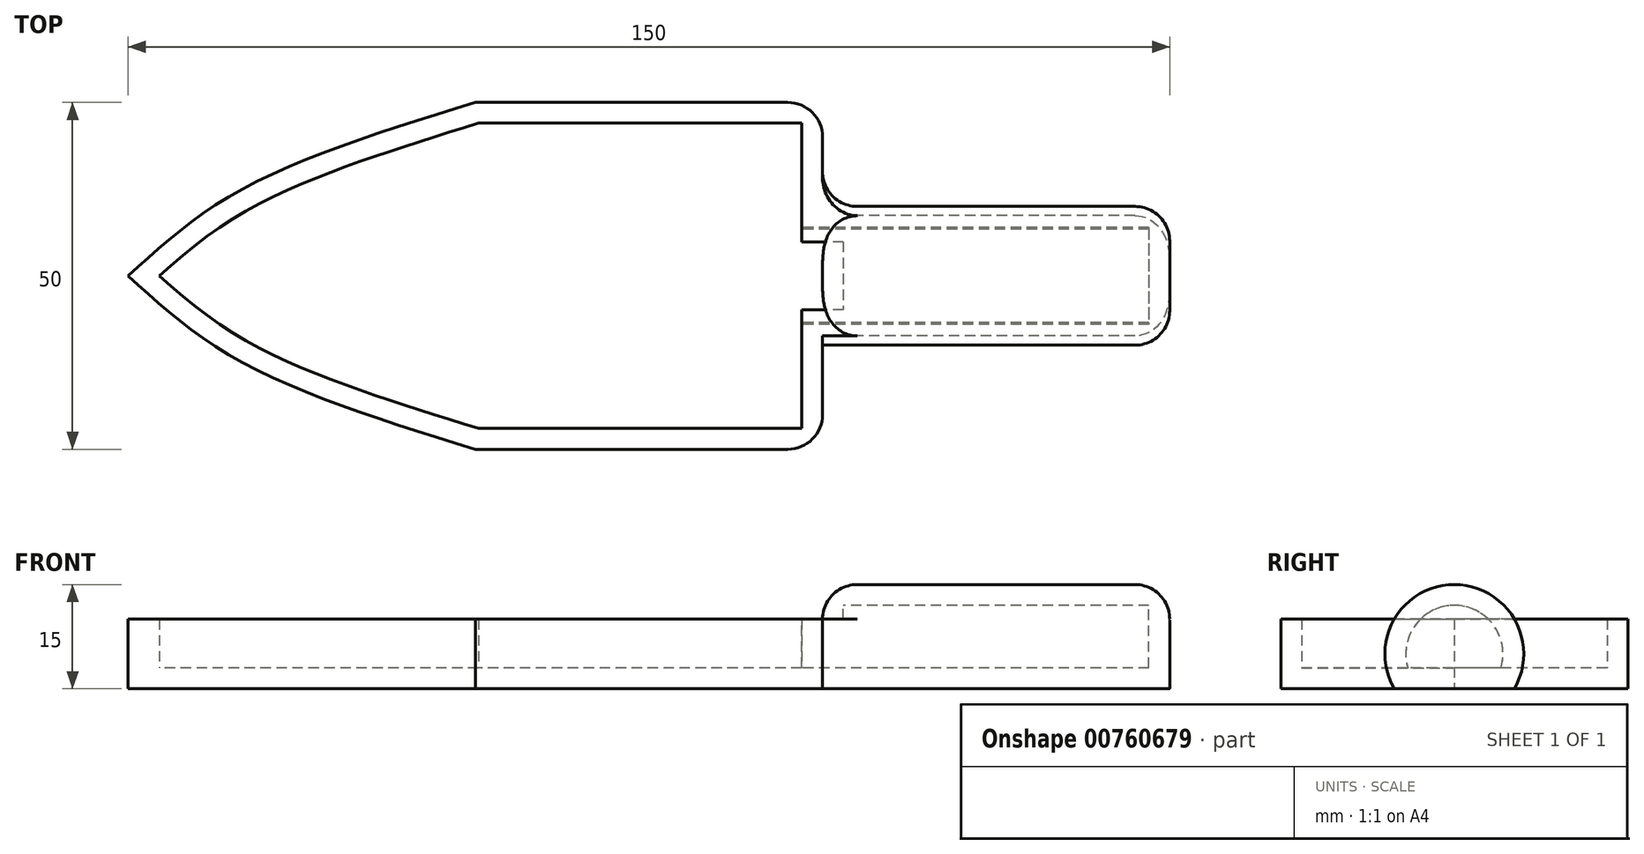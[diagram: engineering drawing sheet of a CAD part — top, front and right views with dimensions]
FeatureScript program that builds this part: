
annotation { "Feature Type Name" : "Feature", "Feature Type Description" : "" }
export const myFeature = defineFeature(function(context is Context, id is Id, definition is map)
    precondition{}
    {
        {
            var Q0;
            Q0=qCreatedBy(makeId("Top.planeOp"),FACE);
            var sketch = newSketch(context, id + "F0", { "sketchPlane" : qUnion([Q0])});
            skLineSegment(sketch, "E0.bottom", {"start": v(50, 25) * mm, "end": v(-50, 25) * mm});
            skLineSegment(sketch, "E0.top", {"start": v(50, -25) * mm, "end": v(-50, -25) * mm});
            skLineSegment(sketch, "E0.left", {"start": v(50, 25) * mm, "end": v(50, -25) * mm});
            skLineSegment(sketch, "E0.right", {"start": v(-50, 25) * mm, "end": v(-50, -25) * mm});
            skPoint(sketch, "E0.middle", {"position": v(0, 0) * mm});
            skFitSpline(sketch, "E1", {"points": [v(0, 25) * mm, v(-33.82, 12.36) * mm, v(-50, 0) * mm], "startDerivative": vector(-65.35, -20.23) * mm, "endDerivative": vector(-33.13, -30.24) * mm});
            skLineSegment(sketch, "E2", {"start": v(-50, 0) * mm, "end": v(50, 0) * mm});
            skFitSpline(sketch, "E3.MirrorCS", {"points": [v(0, -25) * mm, v(-33.82, -12.36) * mm, v(-50, 0) * mm], "startDerivative": vector(-65.35, 20.23) * mm, "endDerivative": vector(-33.13, 30.24) * mm});
            skSolve(sketch);
        }
        {
            var Q0;
            {var subQ3=sQuery(id+"F0.wireOp",EDGE,"E1");Q0=makeQuery(id+"F0.imprint","IMPRINT",FACE,{"disambiguationData":[TD([[makeQuery(id+"F0.imprint","IMPRINT",EDGE,{"derivedFrom":subQ3}),1.0]])]});}
            var Q1;
            {var subQ4=sQuery(id+"F0.wireOp",EDGE,"E2");Q1=makeQuery(id+"F0.imprint","IMPRINT",FACE,{"disambiguationData":[TD([[makeQuery(id+"F0.imprint","IMPRINT",EDGE,{"derivedFrom":subQ4}),-1.0]])]});}
            extrude(context, id + "F1", {"entities" : qUnion([Q0, Q1]), "endBound" : BoundingType.SYMMETRIC, "depth" : 10 * mm, "offsetDistance" : 25 * mm});
        }
        {
            var Q0;
            Q0=makeQuery(id+"F1.opExtrude","SWEPT_FACE",FACE,{"disambiguationData":[OSD([sQuery(id+"F0.wireOp",EDGE,"E0.left")])]});
            var sketch = newSketch(context, id + "F2", { "sketchPlane" : qUnion([Q0])});
            skCircle(sketch, "E4", {"center": v(0, 0) * mm, "radius": 10 * mm});
            skSolve(sketch);
        }
        {
            var Q0;
            {var subQ0=sQuery(id+"F2.wireOp",EDGE,"E4");var subQ1=makeQuery(id+"F1.opExtrude","CAP_EDGE",EDGE,{"disambiguationData":[OSD([sQuery(id+"F0.wireOp",EDGE,"E0.left")])],"isStart":false});var subQ2=makeQuery(id+"F2.imprint","INTERSECT",VERTEX,{"disambiguationData":[OD(0.0)],"derivedFrom":[subQ1,subQ0]});Q0=makeQuery(id+"F2.imprint","IMPRINT",FACE,{"disambiguationData":[TD([[makeQuery(id+"F2.imprint","IMPRINT",EDGE,{"disambiguationData":[TD([[subQ2,1.0]])],"derivedFrom":subQ0}),1.0]])]});}
            var Q1;
            {var subQ0=sQuery(id+"F2.wireOp",EDGE,"E4");var subQ1=sQuery(id+"F0.wireOp",EDGE,"E0.left");var subQ2=makeQuery(id+"F1.opExtrude","CAP_EDGE",EDGE,{"disambiguationData":[OSD([subQ1])],"isStart":false});var subQ3=makeQuery(id+"F2.imprint","INTERSECT",VERTEX,{"disambiguationData":[OD(0.0)],"derivedFrom":[subQ2,subQ0]});Q1=makeQuery(id+"F2.imprint","IMPRINT",FACE,{"disambiguationData":[TD([[makeQuery(id+"F2.imprint","IMPRINT",EDGE,{"disambiguationData":[TD([[subQ3,-1.0]])],"derivedFrom":subQ0}),1.0]])]});}
            var Q2;
            {var subQ0=sQuery(id+"F2.wireOp",EDGE,"E4");var subQ1=makeQuery(id+"F1.opExtrude","CAP_EDGE",EDGE,{"disambiguationData":[OSD([sQuery(id+"F0.wireOp",EDGE,"E0.left")])],"isStart":true});var subQ2=makeQuery(id+"F2.imprint","INTERSECT",VERTEX,{"disambiguationData":[OD(0.0)],"derivedFrom":[subQ1,subQ0]});Q2=makeQuery(id+"F2.imprint","IMPRINT",FACE,{"disambiguationData":[TD([[makeQuery(id+"F2.imprint","IMPRINT",EDGE,{"disambiguationData":[TD([[subQ2,-1.0]])],"derivedFrom":subQ0}),1.0]])]});}
            var Q3;
            Q3=sQuery(id+"F2.wireOp",EDGE,"E4");
            extrude(context, id + "F3", {"entities" : qUnion([Q0, Q1, Q2]), "operationType" : NewBodyOperationType.ADD, "surfaceEntities" : qUnion([Q3]), "depth" : 50 * mm, "offsetDistance" : 25 * mm});
        }
        {
            var Q0;
            Q0=makeQuery(id+"F1.opExtrude","CAP_FACE",FACE,{"disambiguationData":[OSD([sQuery(id+"F0.wireOp",EDGE,"E0.bottom"),sQuery(id+"F0.wireOp",EDGE,"E0.top"),sQuery(id+"F0.wireOp",EDGE,"E0.left"),sQuery(id+"F0.wireOp",EDGE,"E1"),sQuery(id+"F0.wireOp",EDGE,"E3.MirrorCS")])],"isStart":false});
            shell(context, id + "F4", {"entities" : qUnion([Q0]), "thickness" : 3 * mm});
        }
        {
            var Q0;
            Q0=makeQuery(id+"F1.opExtrude","SWEPT_EDGE",EDGE,{"disambiguationData":[OSD([sQuery(id+"F0.wireOp",EDGE,"E0.top"),sQuery(id+"F0.wireOp",EDGE,"E0.left")])]});
            var Q1;
            Q1=makeQuery(id+"F1.opExtrude","SWEPT_EDGE",EDGE,{"disambiguationData":[OSD([sQuery(id+"F0.wireOp",EDGE,"E0.bottom"),sQuery(id+"F0.wireOp",EDGE,"E0.left")])]});
            var Q2;
            {var subQ0=sQuery(id+"F2.wireOp",EDGE,"E4");Q2=makeQuery(id+"F3.boolean.opBoolean","SPLIT",EDGE,{"disambiguationData":[topologyDisambiguationEdgeConnected([makeQuery(id+"F1.opExtrude","SWEPT_FACE",FACE,{"disambiguationData":[OSD([sQuery(id+"F0.wireOp",EDGE,"E0.left")])]}),makeQuery(id+"F3.opExtrude","SWEPT_FACE",FACE,{"disambiguationData":[OSD([subQ0])]})]),OD(0.0)],"derivedFrom":makeQuery(id+"F3.opExtrude","CAP_EDGE",EDGE,{"disambiguationData":[OSD([subQ0])],"isStart":true})});}
            var Q3;
            {var subQ0=sQuery(id+"F2.wireOp",EDGE,"E4");Q3=makeQuery(id+"F3.boolean.opBoolean","SPLIT",EDGE,{"disambiguationData":[topologyDisambiguationEdgeConnected([makeQuery(id+"F1.opExtrude","SWEPT_FACE",FACE,{"disambiguationData":[OSD([sQuery(id+"F0.wireOp",EDGE,"E0.left")])]}),makeQuery(id+"F3.opExtrude","SWEPT_FACE",FACE,{"disambiguationData":[OSD([subQ0])]})]),OD(1.0)],"derivedFrom":makeQuery(id+"F3.opExtrude","CAP_EDGE",EDGE,{"disambiguationData":[OSD([subQ0])],"isStart":true})});}
            var Q4;
            Q4=makeQuery(id+"F3.opExtrude","CAP_EDGE",EDGE,{"disambiguationData":[OSD([sQuery(id+"F2.wireOp",EDGE,"E4")])],"isStart":false});
            fillet(context, id + "F5", {"entities" : qUnion([Q0, Q1, Q2, Q3, Q4]), "radius" : 5 * mm, "tangentPropagation" : true, "allowEdgeOverflow" : false});
        }
        {
            var Q0;
            {var subQ0=sQuery(id+"F0.wireOp",EDGE,"E0.left");var subQ1=sQuery(id+"F2.wireOp",EDGE,"E4");var subQ2=makeQuery(id+"F3.opExtrude","CAP_FACE",FACE,{"disambiguationData":[OSD([subQ1])],"isStart":true});var subQ3=makeQuery(id+"F3.opExtrude","SWEPT_FACE",FACE,{"disambiguationData":[OSD([subQ1])]});Q0=makeQuery(id+"F3.boolean.opBoolean","SPLIT",EDGE,{"disambiguationData":[topologyDisambiguationEdgeConnected([subQ3,subQ2]),TD([makeQuery(id+"F1.opExtrude","CAP_FACE",FACE,{"disambiguationData":[OSD([sQuery(id+"F0.wireOp",EDGE,"E0.bottom"),sQuery(id+"F0.wireOp",EDGE,"E0.top"),subQ0,sQuery(id+"F0.wireOp",EDGE,"E1"),sQuery(id+"F0.wireOp",EDGE,"E3.MirrorCS")])],"isStart":false})])],"derivedFrom":makeQuery(id+"F3.opExtrude","CAP_EDGE",EDGE,{"disambiguationData":[OSD([subQ1])],"isStart":true})});}
            var Q1;
            {var subQ0=sQuery(id+"F0.wireOp",EDGE,"E0.left");var subQ1=sQuery(id+"F2.wireOp",EDGE,"E4");var subQ2=makeQuery(id+"F3.opExtrude","CAP_FACE",FACE,{"disambiguationData":[OSD([subQ1])],"isStart":true});var subQ3=makeQuery(id+"F3.opExtrude","SWEPT_FACE",FACE,{"disambiguationData":[OSD([subQ1])]});Q1=makeQuery(id+"F3.boolean.opBoolean","SPLIT",EDGE,{"disambiguationData":[topologyDisambiguationEdgeConnected([subQ3,subQ2]),TD([makeQuery(id+"F1.opExtrude","CAP_FACE",FACE,{"disambiguationData":[OSD([sQuery(id+"F0.wireOp",EDGE,"E0.bottom"),sQuery(id+"F0.wireOp",EDGE,"E0.top"),subQ0,sQuery(id+"F0.wireOp",EDGE,"E1"),sQuery(id+"F0.wireOp",EDGE,"E3.MirrorCS")])],"isStart":true})])],"derivedFrom":makeQuery(id+"F3.opExtrude","CAP_EDGE",EDGE,{"disambiguationData":[OSD([subQ1])],"isStart":true})});}
            fillet(context, id + "F6", {"entities" : qUnion([Q0, Q1]), "radius" : 5 * mm, "tangentPropagation" : true, "allowEdgeOverflow" : false});
        }
    });
